# Revit family: NBS_COBAFlooring_EntMatt_PathMasterBudget
name_source: partatom
category: Generic Models
revit_build: Autodesk Revit Architecture 2013 (Build: 20130531_2115(x64)
units: mm (PartAtom-declared; Revit-internal decimal feet)

## types (1)
- PathMasterBudget
    Arrangement = Internally inset in a matwell
    AssetType = Fixed
    BIMObjectName = NBS_COBAFlooring_EntranceMatting_PathMasterBudget
    BaseColour = Black
    BaseMaterial = Anti-slip latex backing
    CarpetColourOptions = Charcoal, Grey, Beige, Brown
    Color = Charcoal, Grey, Beige, Brown
    Combustible = No
    Construction = Closed
    Default Elevation = 1200 mm
    Description = Cost effective polypropylene alternative to traditional aluminium entrance matting systems
    EdgingMaterial = NBS_Concept
    EntranceMattingHeight = 13 mm
    EntranceMattingMaterial = NBS_Concept
    EntranceMattingWidth = 2000 mm  [stored 6.56168 ft]
    ExpectedLife = 7 years* If used in the correct environment for the volume and type of traffic expected over the system.
    Finish = Polypropylene carpet strips with aluminium scraping inserts
    FireRating = EN 13501 Euro Classification Ef1
    FlammabilityRating = Class E
    HasAntiStaticSurface = No
    HasNonSkidSurface = Yes
    IfcExportAs = IfcBuildingElementProxyType
    IfcExportType = USERDEFINED
    IsExternal = No
    LinkingJoints = Aluminium
    ManufacturerName = COBA Flooring
    ManufacturerURL = www.cobaeurope.com/flooring/
    Material = Polypropylene needlepunch carpet with aluminium scraping inserts. Anti-slip latex backing.
    MattingHeight = 13 mm
    ModelNumber = PMB
    ModelReference = PathMaster Budget
    NBSCertification = www.nationalbimlibrary.com/cert/hpjvlmzs
    NBSDescription = Entrance matting
    NBSReference = 45-35-35/420
    Name = EntranceMatting_COBAFlooring_PathMasterBudget
    NominalHeight = 13 mm
    NominalWidth = 2000 mm  [stored 6.56168 ft]
    Pattern = Horizontal strips
    ProductInformation = www.cobaeurope.com/entrance-matting-systems/pathmaster-budget-aluminium-matting/
    SurfaceInsertOptions = Charcoal carpet, Grey carpet, Beige carpet, Brown carpet
    ThermalTransmittance = 0
    TrafficType = Pedestrian, wheel chairs, pushchairs and trolleys
    Uniclass2 = 45-57-11/426
    Version = 2
    WarrantyStartDate = 1900-12-31T23:59:59

note: [stored X ft] marks values corroborated as IEEE doubles in the binary element streams (Revit-internal decimal feet)

## geometry (parser evidence)
native form markers: Sweep x1
no freeform markers — native parametric forms only
